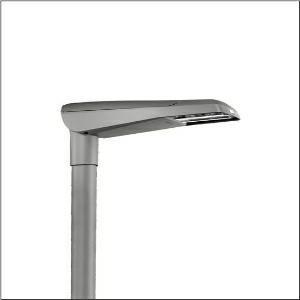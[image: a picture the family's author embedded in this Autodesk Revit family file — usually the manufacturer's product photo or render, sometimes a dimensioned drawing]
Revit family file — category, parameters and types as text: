
# Revit family: streetlight_sl_11_iq_micro___st1_2a_5xc1a51f08ce_9ca9
name_source: partatom
category: Lighting Fixtures
units: mm (PartAtom-declared; Revit-internal decimal feet)

## family parameters
Cut with Voids When Loaded = No
Host = Face
Light Source = No
Part Type = Normal
Room Calculation Point = No
Round Connector Dimension = Use Diameter
Shared = No

## types (1)
- --- (1 x LED, 1880 lm, 12.6 W, 3000K)
    Apparent Load = 13 VA
    CIE Flux Codes = 33 71 96 100 100
    Color Rendering = 70
    Color Temperature = 3000K
    Default Elevation = 1800 mm
    Description = Streetlight SL 11 iQ micro, mast luminaire, primary light control with 3 zone facetted reflector, of plastic, silver coated, highly specular, primary optical cover: cover, of PMMA, transparent, light distribution: ST1.2a, light emission: direct distribution, primary light characteristic: asymmetric, installation type: post-top, side-entry, lamps: LED, High Power LED, rated values: 1.880lm | 12,6W | 149,2lm/W (begin service life); end service life: 1.880lm | 12,9W; at 50% lumin. flux: 940lm | 6,8W | 138,2lm/W, colour temperature: 3000K, colour rendering: CRI > 70, light colour: 730, light setting 1 begin service life: 100% | 1.880lm | 12,6W | 149,2lm/W | 3.000K, light setting 1 end service life: 12,9W, further light settings possible, control: Street-Remote, optimised constant luminous flux control (CLO 2.0), Desk-Remote (wireless, voltage-free reading and setting of iQ features in the workshop via application-optimized NFC function/RFID function), Light-Fading, Smart-Wire, Night-Set, Lumen-Switch, Temp-Guard, Auto-Match, with cable H07RN-F 3x 1.5mm², mains connection: 230..240V, AC, 50/60Hz, connection cable pre-assembled, cable length: 5,5m, luminaire housing, of diecast aluminium, powder-coated, SITECO metallic grey (DB 702S), please order mast flange separately, inclination adjustable without tools: 0°, 5°, 10°, 15° (post-top) | 0°, -5°, -10°, -15° (side-entry), sealing non-destructively replaceable, multi-level sealing system, length: 600mm, width: 174mm, height: 116mm, mast flange for spigot size: 42mm (side-entry): 5XC10008XM4, 60/48mm (side-entry/post-top): 5XC10108XM2, 76/60mm (side-entry/post-top): 5XC10108XM1, equipment: standard, protection rating (complete): IP66, insulation class (complete): insulation class II (safety insulation), certification: CE, ENEC, ENEC+, VDE, impact resistance: IK10, permissible operating ambient temperature for outdoor applications: -25..+50°C, standard-compliant lighting for roads and squares, Environmental Product Declaration (EPD) tested and certified by an independent institute, packaging unit: 1 piece

Light Distribution: ST1.2a
    Height = 116 mm
    Lamp = 1 x LED
    Lamp Light Flux = 1880 lm
    Lamp Power = 12.6 W
    Lamp count = 1
    Length = 600 mm
    Luminous efficacy = 149 lm/W
    Manufacturer = Siteco
    ModVariant = No
    Model = 5XC1A51F08CE
    Number of Poles = 1
    OnlyDefault = Yes
    Power Factor = 1
    Product Name = Streetlight SL 11 iQ micro | ST1.2a
    Product group = mast luminaire | pylon top
    ProductGroupID = 6100
    Protection Class = Protection class II
    Protection Degree = IP 66
    RLX_Detail_Level = 1
    RLX_Emergency_Light_Flux = 0 lm
    RLX_Emergency_Type = 0
    RLX_Emergency_Type_DB = No
    RlxData = <blob elided: 26489 chars, md5=4a80b672>
    Socket = socket
    Standby Power = 0 W
    System Light Flux = 1880 lm
    System Power = 13 W
    Type Comments = factory setting: luminous flux: 100 % | dim-lin: 254 | 229 mA
    Type Image = l_1006566.jpg
    URL = http://relux.com
    VarID = @adj_019107
    Voltage = 0 V
    Weight = 0.00 kg
    Width = 174 mm

## geometry (parser evidence)
native form markers: Blend x4, Sweep x11
no freeform markers — native parametric forms only
